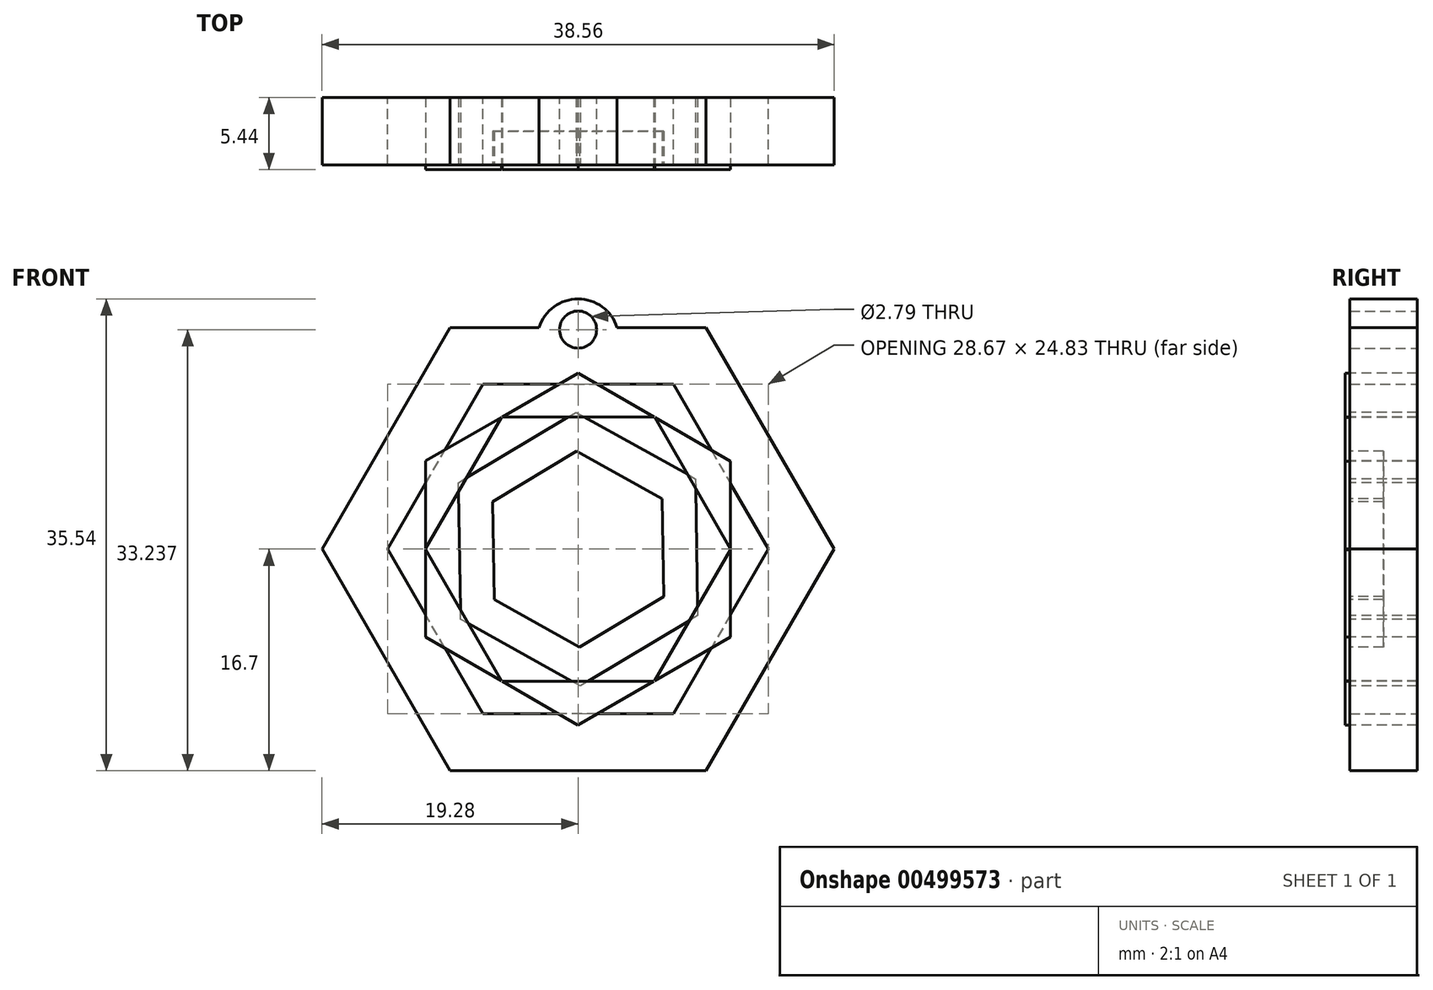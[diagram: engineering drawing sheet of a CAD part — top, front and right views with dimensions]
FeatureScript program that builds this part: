
annotation { "Feature Type Name" : "Feature", "Feature Type Description" : "" }
export const myFeature = defineFeature(function(context is Context, id is Id, definition is map)
    precondition{}
    {
        {
            var Q0;
            Q0=qCreatedBy(makeId("Front.planeOp"),FACE);
            var sketch = newSketch(context, id + "F0", { "sketchPlane" : qUnion([Q0])});
            skCircle(sketch, "E0.cCircle", {"center": v(0, 0) * mm, "radius": 16.7 * mm, "construction": true});
            skLineSegment(sketch, "E0.0", {"start": v(9.64, -16.7) * mm, "end": v(-9.64, -16.7) * mm});
            skLineSegment(sketch, "E0.1", {"start": v(-9.64, -16.7) * mm, "end": v(-19.28, 0) * mm});
            skLineSegment(sketch, "E0.2", {"start": v(-19.28, 0) * mm, "end": v(-9.64, 16.7) * mm});
            skLineSegment(sketch, "E0.3", {"start": v(-9.64, 16.7) * mm, "end": v(9.64, 16.7) * mm});
            skLineSegment(sketch, "E0.4", {"start": v(9.64, 16.7) * mm, "end": v(19.28, 0) * mm});
            skLineSegment(sketch, "E0.5", {"start": v(19.28, 0) * mm, "end": v(9.64, -16.7) * mm});
            skPoint(sketch, "E0.0.midPoint", {"position": v(0, -16.7) * mm});
            skCircle(sketch, "E1.cCircle", {"center": v(0, 0) * mm, "radius": 12.42 * mm, "construction": true});
            skLineSegment(sketch, "E1.0", {"start": v(7.17, -12.42) * mm, "end": v(-7.17, -12.42) * mm});
            skLineSegment(sketch, "E1.1", {"start": v(-7.17, -12.42) * mm, "end": v(-14.34, 0) * mm});
            skLineSegment(sketch, "E1.2", {"start": v(-14.34, 0) * mm, "end": v(-7.17, 12.42) * mm});
            skLineSegment(sketch, "E1.3", {"start": v(-7.17, 12.42) * mm, "end": v(7.17, 12.42) * mm});
            skLineSegment(sketch, "E1.4", {"start": v(7.17, 12.42) * mm, "end": v(14.34, 0) * mm});
            skLineSegment(sketch, "E1.5", {"start": v(14.34, 0) * mm, "end": v(7.17, -12.42) * mm});
            skPoint(sketch, "E1.0.midPoint", {"position": v(0, -12.42) * mm});
            skSolve(sketch);
        }
        {
            var Q0;
            Q0=makeQuery(id+"F0.imprint","IMPRINT",FACE,{"disambiguationData":[TD([[makeQuery(id+"F0.imprint","IMPRINT",EDGE,{"derivedFrom":sQuery(id+"F0.wireOp",EDGE,"E0.0")}),-1.0]])]});
            extrude(context, id + "F1", {"entities" : qUnion([Q0]), "depth" : 5.08 * mm});
        }
        {
            var Q0;
            Q0=qCreatedBy(makeId("Front.planeOp"),FACE);
            var sketch = newSketch(context, id + "F2", { "sketchPlane" : qUnion([Q0])});
            skCircle(sketch, "E2", {"center": v(0, 15.77) * mm, "radius": 3.08 * mm});
            skSolve(sketch);
        }
        {
            var Q0;
            Q0=makeQuery(id+"F2.imprint","IMPRINT",FACE,{"disambiguationData":[TD([[makeQuery(id+"F2.imprint","IMPRINT",EDGE,{"derivedFrom":sQuery(id+"F2.wireOp",EDGE,"E2")}),1.0]])]});
            extrude(context, id + "F3", {"entities" : qUnion([Q0]), "operationType" : NewBodyOperationType.ADD, "depth" : 5.08 * mm});
        }
        {
            var Q0;
            Q0=qCreatedBy(makeId("Front.planeOp"),FACE);
            var sketch = newSketch(context, id + "F4", { "sketchPlane" : qUnion([Q0])});
            skPoint(sketch, "E3", {"position": v(0, 16.54) * mm});
            skSolve(sketch);
        }
        {
            var Q0;
            Q0=sQuery(id+"F4.wireOp",VERTEX,"E3");
            var Q1;
            Q1=makeQuery(id+"F1.opExtrude","SWEPT_BODY",BODY,{"disambiguationData":[OSD([sQuery(id+"F0.wireOp",EDGE,"E0.0"),sQuery(id+"F0.wireOp",EDGE,"E0.1"),sQuery(id+"F0.wireOp",EDGE,"E0.2"),sQuery(id+"F0.wireOp",EDGE,"E0.3"),sQuery(id+"F0.wireOp",EDGE,"E0.4"),sQuery(id+"F0.wireOp",EDGE,"E0.5"),sQuery(id+"F0.wireOp",EDGE,"E1.0"),sQuery(id+"F0.wireOp",EDGE,"E1.1"),sQuery(id+"F0.wireOp",EDGE,"E1.2"),sQuery(id+"F0.wireOp",EDGE,"E1.3"),sQuery(id+"F0.wireOp",EDGE,"E1.4"),sQuery(id+"F0.wireOp",EDGE,"E1.5")])]});
            hole(context, id + "F5", {"style" : HoleStyle.SIMPLE, "endStyle" : HoleEndStyle.THROUGH, "oppositeDirection" : true, "holeDiameter" : 2.8 * mm, "isTappedThrough" : true, "tappedDepth" : 12.7 * mm, "tapClearance" : 3, "locations" : qUnion([Q0]), "scope" : qUnion([Q1])});
        }
        {
            var Q0;
            Q0=makeQuery(id+"F3.boolean.opBoolean","MERGE",FACE,{"derivedFrom":[makeQuery(id+"F1.opExtrude","CAP_FACE",FACE,{"disambiguationData":[OSD([sQuery(id+"F0.wireOp",EDGE,"E0.0"),sQuery(id+"F0.wireOp",EDGE,"E0.1"),sQuery(id+"F0.wireOp",EDGE,"E0.2"),sQuery(id+"F0.wireOp",EDGE,"E0.3"),sQuery(id+"F0.wireOp",EDGE,"E0.4"),sQuery(id+"F0.wireOp",EDGE,"E0.5"),sQuery(id+"F0.wireOp",EDGE,"E1.0"),sQuery(id+"F0.wireOp",EDGE,"E1.1"),sQuery(id+"F0.wireOp",EDGE,"E1.2"),sQuery(id+"F0.wireOp",EDGE,"E1.3"),sQuery(id+"F0.wireOp",EDGE,"E1.4"),sQuery(id+"F0.wireOp",EDGE,"E1.5")])],"isStart":false}),makeQuery(id+"F3.opExtrude","CAP_FACE",FACE,{"disambiguationData":[OSD([sQuery(id+"F2.wireOp",EDGE,"E2")])],"isStart":false})]});
            var sketch = newSketch(context, id + "F6", { "sketchPlane" : qUnion([Q0])});
            skCircle(sketch, "E4.cCircle", {"center": v(0, 0) * mm, "radius": 10.73 * mm, "construction": true});
            skLineSegment(sketch, "E4.0", {"start": v(0, 12.39) * mm, "end": v(10.73, 6.19) * mm});
            skLineSegment(sketch, "E4.1", {"start": v(10.73, 6.19) * mm, "end": v(10.72, -6.2) * mm});
            skLineSegment(sketch, "E4.2", {"start": v(10.72, -6.2) * mm, "end": v(0, -12.39) * mm});
            skLineSegment(sketch, "E4.3", {"start": v(0, -12.39) * mm, "end": v(-10.73, -6.19) * mm});
            skLineSegment(sketch, "E4.4", {"start": v(-10.73, -6.19) * mm, "end": v(-10.72, 6.2) * mm});
            skLineSegment(sketch, "E4.5", {"start": v(-10.72, 6.2) * mm, "end": v(0, 12.39) * mm});
            skPoint(sketch, "E4.0.midPoint", {"position": v(5.37, 9.29) * mm});
            skCircle(sketch, "E5.cCircle", {"center": v(0, 0) * mm, "radius": 9.3 * mm, "construction": true});
            skLineSegment(sketch, "E5.0", {"start": v(5.38, 9.3) * mm, "end": v(10.75, 0) * mm});
            skLineSegment(sketch, "E5.1", {"start": v(10.75, 0) * mm, "end": v(5.37, -9.31) * mm});
            skLineSegment(sketch, "E5.2", {"start": v(5.37, -9.31) * mm, "end": v(-5.38, -9.3) * mm});
            skLineSegment(sketch, "E5.3", {"start": v(-5.38, -9.3) * mm, "end": v(-10.75, 0) * mm});
            skLineSegment(sketch, "E5.4", {"start": v(-10.75, 0) * mm, "end": v(-5.37, 9.31) * mm});
            skLineSegment(sketch, "E5.5", {"start": v(-5.37, 9.31) * mm, "end": v(5.38, 9.3) * mm});
            skPoint(sketch, "E5.0.midPoint", {"position": v(8.06, 4.65) * mm});
            skCircle(sketch, "E6.cCircle", {"center": v(0, 0) * mm, "radius": 8.04 * mm, "construction": true});
            skLineSegment(sketch, "E6.0", {"start": v(-8.04, 4.65) * mm, "end": v(0, 9.28) * mm});
            skLineSegment(sketch, "E6.1", {"start": v(0, 9.28) * mm, "end": v(8.04, 4.64) * mm});
            skLineSegment(sketch, "E6.2", {"start": v(8.04, 4.64) * mm, "end": v(8.04, -4.65) * mm});
            skLineSegment(sketch, "E6.3", {"start": v(8.04, -4.65) * mm, "end": v(0, -9.28) * mm});
            skLineSegment(sketch, "E6.4", {"start": v(0, -9.28) * mm, "end": v(-8.04, -4.64) * mm});
            skLineSegment(sketch, "E6.5", {"start": v(-8.04, -4.64) * mm, "end": v(-8.04, 4.65) * mm});
            skPoint(sketch, "E6.0.midPoint", {"position": v(-4.01, 6.97) * mm});
            skCircle(sketch, "E7.cCircle", {"center": v(0, 0) * mm, "radius": 6.97 * mm, "construction": true});
            skLineSegment(sketch, "E7.0", {"start": v(-4.02, 6.97) * mm, "end": v(4.02, 6.97) * mm});
            skLineSegment(sketch, "E7.1", {"start": v(4.02, 6.97) * mm, "end": v(8.04, 0) * mm});
            skLineSegment(sketch, "E7.2", {"start": v(8.04, 0) * mm, "end": v(4.02, -6.97) * mm});
            skLineSegment(sketch, "E7.3", {"start": v(4.02, -6.97) * mm, "end": v(-4.02, -6.97) * mm});
            skLineSegment(sketch, "E7.4", {"start": v(-4.02, -6.97) * mm, "end": v(-8.04, 0) * mm});
            skLineSegment(sketch, "E7.5", {"start": v(-8.04, 0) * mm, "end": v(-4.02, 6.97) * mm});
            skPoint(sketch, "E7.0.midPoint", {"position": v(0, 6.97) * mm});
            skSolve(sketch);
        }
        {
            var Q0;
            {var subQ0=sQuery(id+"F6.wireOp",EDGE,"E4.5");var subQ1=sQuery(id+"F6.wireOp",EDGE,"E4.0");var subQ2=makeQuery(id+"F6.imprint","INTERSECT",VERTEX,{"derivedFrom":[subQ1,subQ0]});Q0=makeQuery(id+"F6.imprint","IMPRINT",FACE,{"disambiguationData":[TD([[makeQuery(id+"F6.imprint","IMPRINT",EDGE,{"disambiguationData":[TD([[subQ2,-1.0]])],"derivedFrom":subQ1}),-1.0]])]});}
            var Q1;
            {var subQ0=sQuery(id+"F6.wireOp",EDGE,"E4.5");var subQ1=sQuery(id+"F6.wireOp",EDGE,"E4.4");var subQ2=makeQuery(id+"F6.imprint","INTERSECT",VERTEX,{"derivedFrom":[subQ1,subQ0]});Q1=makeQuery(id+"F6.imprint","IMPRINT",FACE,{"disambiguationData":[TD([[makeQuery(id+"F6.imprint","IMPRINT",EDGE,{"disambiguationData":[TD([[subQ2,1.0]])],"derivedFrom":subQ1}),-1.0]])]});}
            var Q2;
            {var subQ0=sQuery(id+"F6.wireOp",EDGE,"E4.4");var subQ1=sQuery(id+"F6.wireOp",EDGE,"E4.3");var subQ2=makeQuery(id+"F6.imprint","INTERSECT",VERTEX,{"derivedFrom":[subQ1,subQ0]});Q2=makeQuery(id+"F6.imprint","IMPRINT",FACE,{"disambiguationData":[TD([[makeQuery(id+"F6.imprint","IMPRINT",EDGE,{"disambiguationData":[TD([[subQ2,1.0]])],"derivedFrom":subQ1}),-1.0]])]});}
            var Q3;
            {var subQ14=sQuery(id+"F6.wireOp",EDGE,"E6.0");var subQ20=sQuery(id+"F6.wireOp",EDGE,"E7.5");var subQ23=makeQuery(id+"F6.imprint","INTERSECT",VERTEX,{"derivedFrom":[subQ14,subQ20]});Q3=makeQuery(id+"F6.imprint","IMPRINT",FACE,{"disambiguationData":[TD([[makeQuery(id+"F6.imprint","IMPRINT",EDGE,{"disambiguationData":[TD([[subQ23,-1.0]])],"derivedFrom":subQ14}),-1.0]])]});}
            var Q4;
            {var subQ0=sQuery(id+"F6.wireOp",EDGE,"E4.1");var subQ1=sQuery(id+"F6.wireOp",EDGE,"E4.0");var subQ2=makeQuery(id+"F6.imprint","INTERSECT",VERTEX,{"derivedFrom":[subQ1,subQ0]});Q4=makeQuery(id+"F6.imprint","IMPRINT",FACE,{"disambiguationData":[TD([[makeQuery(id+"F6.imprint","IMPRINT",EDGE,{"disambiguationData":[TD([[subQ2,1.0]])],"derivedFrom":subQ1}),-1.0]])]});}
            var Q5;
            {var subQ0=sQuery(id+"F6.wireOp",EDGE,"E4.2");var subQ1=sQuery(id+"F6.wireOp",EDGE,"E4.1");var subQ2=makeQuery(id+"F6.imprint","INTERSECT",VERTEX,{"derivedFrom":[subQ1,subQ0]});Q5=makeQuery(id+"F6.imprint","IMPRINT",FACE,{"disambiguationData":[TD([[makeQuery(id+"F6.imprint","IMPRINT",EDGE,{"disambiguationData":[TD([[subQ2,1.0]])],"derivedFrom":subQ1}),-1.0]])]});}
            var Q6;
            {var subQ0=sQuery(id+"F6.wireOp",EDGE,"E4.3");var subQ1=sQuery(id+"F6.wireOp",EDGE,"E4.2");var subQ2=makeQuery(id+"F6.imprint","INTERSECT",VERTEX,{"derivedFrom":[subQ1,subQ0]});Q6=makeQuery(id+"F6.imprint","IMPRINT",FACE,{"disambiguationData":[TD([[makeQuery(id+"F6.imprint","IMPRINT",EDGE,{"disambiguationData":[TD([[subQ2,1.0]])],"derivedFrom":subQ1}),-1.0]])]});}
            extrude(context, id + "F7", {"entities" : qUnion([Q0, Q1, Q2, Q3, Q4, Q5, Q6]), "oppositeDirection" : true, "depth" : 5.08 * mm});
        }
        {
            var Q0;
            Q0=makeQuery(id+"F7.opExtrude","SWEPT_BODY",BODY,{"disambiguationData":[OSD([sQuery(id+"F6.wireOp",EDGE,"E4.0"),sQuery(id+"F6.wireOp",EDGE,"E4.1"),sQuery(id+"F6.wireOp",EDGE,"E5.0")])]});
            var Q1;
            Q1=makeQuery(id+"F7.opExtrude","SWEPT_BODY",BODY,{"disambiguationData":[OSD([sQuery(id+"F6.wireOp",EDGE,"E4.1"),sQuery(id+"F6.wireOp",EDGE,"E4.2"),sQuery(id+"F6.wireOp",EDGE,"E5.1")])]});
            var Q2;
            Q2=makeQuery(id+"F7.opExtrude","SWEPT_BODY",BODY,{"disambiguationData":[OSD([sQuery(id+"F6.wireOp",EDGE,"E4.2"),sQuery(id+"F6.wireOp",EDGE,"E4.3"),sQuery(id+"F6.wireOp",EDGE,"E5.2")])]});
            var Q3;
            Q3=makeQuery(id+"F7.opExtrude","SWEPT_BODY",BODY,{"disambiguationData":[OSD([sQuery(id+"F6.wireOp",EDGE,"E4.3"),sQuery(id+"F6.wireOp",EDGE,"E4.4"),sQuery(id+"F6.wireOp",EDGE,"E5.3")])]});
            var Q4;
            Q4=makeQuery(id+"F7.opExtrude","SWEPT_BODY",BODY,{"disambiguationData":[OSD([sQuery(id+"F6.wireOp",EDGE,"E4.4"),sQuery(id+"F6.wireOp",EDGE,"E4.5"),sQuery(id+"F6.wireOp",EDGE,"E5.4")])]});
            var Q5;
            Q5=makeQuery(id+"F7.opExtrude","SWEPT_BODY",BODY,{"disambiguationData":[OSD([sQuery(id+"F6.wireOp",EDGE,"E4.0"),sQuery(id+"F6.wireOp",EDGE,"E4.5"),sQuery(id+"F6.wireOp",EDGE,"E5.5")])]});
            var Q6;
            Q6=qCreatedBy(makeId("Origin.pointOp"),VERTEX);
            transform(context, id + "F8", {"entities" : qUnion([Q0, Q1, Q2, Q3, Q4, Q5]), "transformType" : TransformType.SCALE_UNIFORMLY, "scale" : 1.07, "scalePoint" : qUnion([Q6]), "makeCopy" : false});
        }
        {
            var Q0;
            Q0=makeQuery(id+"F7.opExtrude","CAP_FACE",FACE,{"disambiguationData":[OSD([sQuery(id+"F6.wireOp",EDGE,"E6.0"),sQuery(id+"F6.wireOp",EDGE,"E6.1"),sQuery(id+"F6.wireOp",EDGE,"E6.2"),sQuery(id+"F6.wireOp",EDGE,"E6.3"),sQuery(id+"F6.wireOp",EDGE,"E6.4"),sQuery(id+"F6.wireOp",EDGE,"E6.5"),sQuery(id+"F6.wireOp",EDGE,"E7.0"),sQuery(id+"F6.wireOp",EDGE,"E7.1"),sQuery(id+"F6.wireOp",EDGE,"E7.2"),sQuery(id+"F6.wireOp",EDGE,"E7.3"),sQuery(id+"F6.wireOp",EDGE,"E7.4"),sQuery(id+"F6.wireOp",EDGE,"E7.5")])],"isStart":true});
            var sketch = newSketch(context, id + "F9", { "sketchPlane" : qUnion([Q0])});
            skPoint(sketch, "E8", {"position": v(0, 0) * mm});
            skCircle(sketch, "E9.cCircle", {"center": v(0, 0) * mm, "radius": 8.93 * mm, "construction": true});
            skLineSegment(sketch, "E9.0", {"start": v(9, -5) * mm, "end": v(0.17, -10.3) * mm});
            skLineSegment(sketch, "E9.1", {"start": v(0.17, -10.3) * mm, "end": v(-8.84, -5.3) * mm});
            skLineSegment(sketch, "E9.2", {"start": v(-8.84, -5.3) * mm, "end": v(-9, 5) * mm});
            skLineSegment(sketch, "E9.3", {"start": v(-9, 5) * mm, "end": v(-0.17, 10.3) * mm});
            skLineSegment(sketch, "E9.4", {"start": v(-0.17, 10.3) * mm, "end": v(8.84, 5.3) * mm});
            skLineSegment(sketch, "E9.5", {"start": v(8.84, 5.3) * mm, "end": v(9, -5) * mm});
            skPoint(sketch, "E9.0.midPoint", {"position": v(4.59, -7.66) * mm});
            skSolve(sketch);
        }
        {
            var Q0;
            Q0=qSketchRegion(id+"F9",true);
            extrude(context, id + "F10", {"entities" : qUnion([Q0]), "oppositeDirection" : true, "depth" : 5.08 * mm});
        }
        {
            var Q0;
            Q0=makeQuery(id+"F7.opExtrude","CAP_FACE",FACE,{"disambiguationData":[OSD([sQuery(id+"F6.wireOp",EDGE,"E6.0"),sQuery(id+"F6.wireOp",EDGE,"E6.1"),sQuery(id+"F6.wireOp",EDGE,"E6.2"),sQuery(id+"F6.wireOp",EDGE,"E6.3"),sQuery(id+"F6.wireOp",EDGE,"E6.4"),sQuery(id+"F6.wireOp",EDGE,"E6.5"),sQuery(id+"F6.wireOp",EDGE,"E7.0"),sQuery(id+"F6.wireOp",EDGE,"E7.1"),sQuery(id+"F6.wireOp",EDGE,"E7.2"),sQuery(id+"F6.wireOp",EDGE,"E7.3"),sQuery(id+"F6.wireOp",EDGE,"E7.4"),sQuery(id+"F6.wireOp",EDGE,"E7.5")])],"isStart":true});
            extrude(context, id + "F11", {"entities" : qUnion([Q0]), "oppositeDirection" : true, "depth" : 1.5 * mm});
        }
        {
            var Q0;
            Q0=makeQuery(id+"F7.opExtrude","SWEPT_BODY",BODY,{"disambiguationData":[OSD([sQuery(id+"F6.wireOp",EDGE,"E6.0"),sQuery(id+"F6.wireOp",EDGE,"E6.1"),sQuery(id+"F6.wireOp",EDGE,"E6.2"),sQuery(id+"F6.wireOp",EDGE,"E6.3"),sQuery(id+"F6.wireOp",EDGE,"E6.4"),sQuery(id+"F6.wireOp",EDGE,"E6.5"),sQuery(id+"F6.wireOp",EDGE,"E7.0"),sQuery(id+"F6.wireOp",EDGE,"E7.1"),sQuery(id+"F6.wireOp",EDGE,"E7.2"),sQuery(id+"F6.wireOp",EDGE,"E7.3"),sQuery(id+"F6.wireOp",EDGE,"E7.4"),sQuery(id+"F6.wireOp",EDGE,"E7.5")])]});
            deleteBodies(context, id + "F12", {"entities" : qUnion([Q0])});
        }
        {
            var Q0;
            Q0=makeQuery(id+"F11.opExtrude","SWEPT_BODY",BODY,{"disambiguationData":[OSD([sQuery(id+"F6.wireOp",EDGE,"E6.0"),sQuery(id+"F6.wireOp",EDGE,"E6.1"),sQuery(id+"F6.wireOp",EDGE,"E6.2"),sQuery(id+"F6.wireOp",EDGE,"E6.3"),sQuery(id+"F6.wireOp",EDGE,"E6.4"),sQuery(id+"F6.wireOp",EDGE,"E6.5"),sQuery(id+"F6.wireOp",EDGE,"E7.0"),sQuery(id+"F6.wireOp",EDGE,"E7.1"),sQuery(id+"F6.wireOp",EDGE,"E7.2"),sQuery(id+"F6.wireOp",EDGE,"E7.3"),sQuery(id+"F6.wireOp",EDGE,"E7.4"),sQuery(id+"F6.wireOp",EDGE,"E7.5")])]});
            deleteBodies(context, id + "F13", {"entities" : qUnion([Q0])});
        }
        {
            var Q0;
            Q0=makeQuery(id+"F10.opExtrude","CAP_FACE",FACE,{"disambiguationData":[OSD([sQuery(id+"F9.wireOp",EDGE,"E9.0"),sQuery(id+"F9.wireOp",EDGE,"E9.1"),sQuery(id+"F9.wireOp",EDGE,"E9.2"),sQuery(id+"F9.wireOp",EDGE,"E9.3"),sQuery(id+"F9.wireOp",EDGE,"E9.4"),sQuery(id+"F9.wireOp",EDGE,"E9.5")])],"isStart":true});
            shell(context, id + "F14", {"entities" : qUnion([Q0]), "thickness" : 2.54 * mm});
        }
    });
